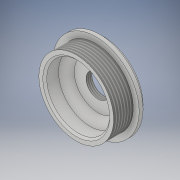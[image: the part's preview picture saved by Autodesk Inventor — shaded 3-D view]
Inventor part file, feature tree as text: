
AUTODESK INVENTOR PART (.ipt)
format: ipt  version: 2019 (Build 230136000, 136)  size: 147,968 bytes
history: native  units: mm
features: other x3, chamfer x3, sketch x1
ambient origin geometry x8: Origin, YZ Plane, XZ Plane, XY Plane, X Axis, Y Axis, Z Axis, Center Point
bodies: Solide1 (feature_tree)
feature tree (7):
  other  "Révolution1"
  chamfer  "Chanfrein1"  Distance=4.0mm
  chamfer  "Chanfrein2"  Distance=10.0mm
  other  "Filetage1"
  chamfer  "Chanfrein3"  Distance=3.0mm
  other  "Filetage2"
  sketch  "Esquisse1"
